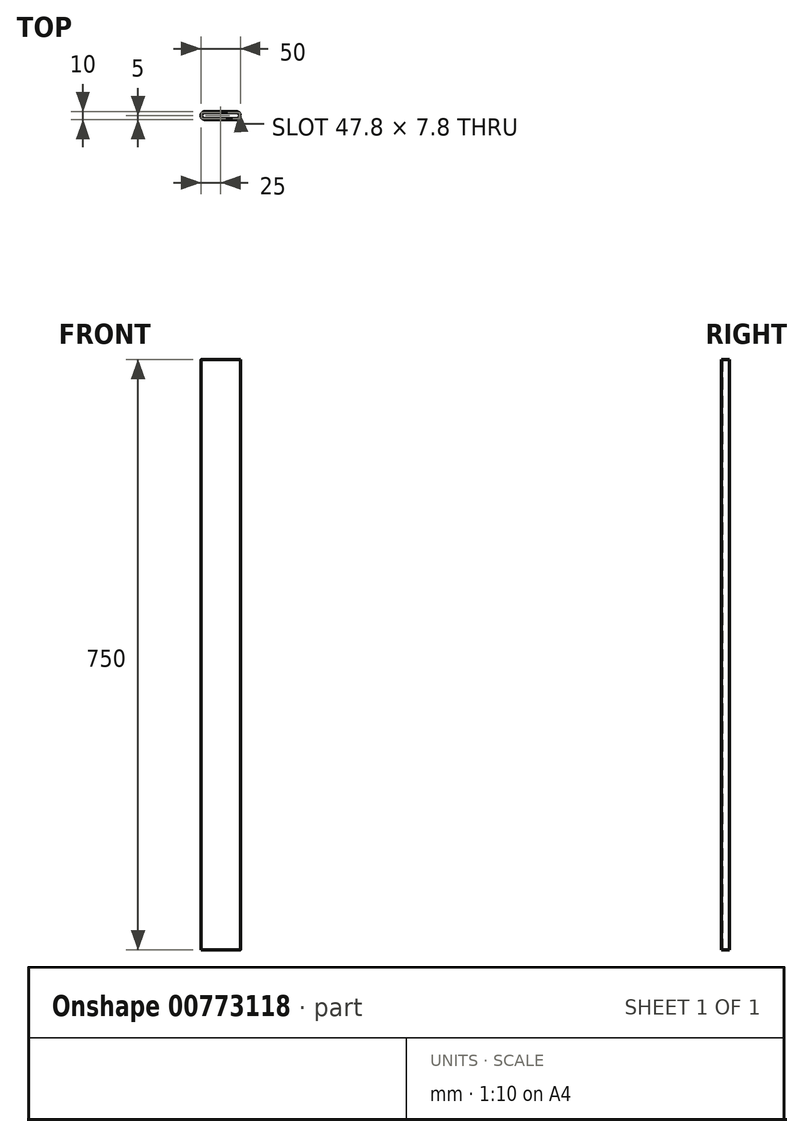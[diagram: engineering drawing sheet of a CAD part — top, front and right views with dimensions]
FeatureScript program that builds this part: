
annotation { "Feature Type Name" : "Feature", "Feature Type Description" : "" }
export const myFeature = defineFeature(function(context is Context, id is Id, definition is map)
    precondition{}
    {
        {
            var Q0;
            Q0=qCreatedBy(makeId("Top.planeOp"),FACE);
            var sketch = newSketch(context, id + "F0", { "sketchPlane" : qUnion([Q0])});
            skLineSegment(sketch, "E0.bottom", {"start": v(-20, 5) * mm, "end": v(20, 5) * mm});
            skLineSegment(sketch, "E0.top", {"start": v(-20, -5) * mm, "end": v(20, -5) * mm});
            skLineSegment(sketch, "E0.left", {"start": v(-25, 0) * mm, "end": v(-25, 0) * mm});
            skLineSegment(sketch, "E0.right", {"start": v(25, 0) * mm, "end": v(25, 0) * mm});
            skPoint(sketch, "E0.middle", {"position": v(0, 0) * mm});
            skPoint(sketch, "E1.visualSharp", {"position": v(-25, 5) * mm});
            skArc(sketch, "E1.filletArc", {"start": v(-20, 5) * mm, "mid": v(-23.54, 3.54) * mm, "end": v(-25, 0) * mm});
            skPoint(sketch, "E2.visualSharp", {"position": v(-25, -5) * mm});
            skArc(sketch, "E2.filletArc", {"start": v(-25, 0) * mm, "mid": v(-23.54, -3.54) * mm, "end": v(-20, -5) * mm});
            skPoint(sketch, "E3.visualSharp", {"position": v(25, 5) * mm});
            skArc(sketch, "E3.filletArc", {"start": v(25, 0) * mm, "mid": v(23.54, 3.54) * mm, "end": v(20, 5) * mm});
            skPoint(sketch, "E4.visualSharp", {"position": v(25, -5) * mm});
            skArc(sketch, "E4.filletArc", {"start": v(20, -5) * mm, "mid": v(23.54, -3.54) * mm, "end": v(25, 0) * mm});
            skArc(sketch, "E5.0", {"start": v(-20, 3.9) * mm, "mid": v(-22.76, 2.76) * mm, "end": v(-23.9, 0) * mm});
            skArc(sketch, "E5.1", {"start": v(23.9, 0) * mm, "mid": v(22.76, 2.76) * mm, "end": v(20, 3.9) * mm});
            skArc(sketch, "E5.2", {"start": v(20, -3.9) * mm, "mid": v(22.76, -2.76) * mm, "end": v(23.9, 0) * mm});
            skLineSegment(sketch, "E5.3", {"start": v(-20, 3.9) * mm, "end": v(20, 3.9) * mm});
            skLineSegment(sketch, "E5.4", {"start": v(-20, -3.9) * mm, "end": v(20, -3.9) * mm});
            skArc(sketch, "E5.5", {"start": v(-23.9, 0) * mm, "mid": v(-22.76, -2.76) * mm, "end": v(-20, -3.9) * mm});
            skSolve(sketch);
        }
        {
            var Q0;
            Q0 = qSketchRegion(id + "F0", true);
            extrude(context, id + "F1", {"entities" : qUnion([Q0]), "depth" : 750 * mm, "offsetDistance" : 25 * mm});
        }
    });
